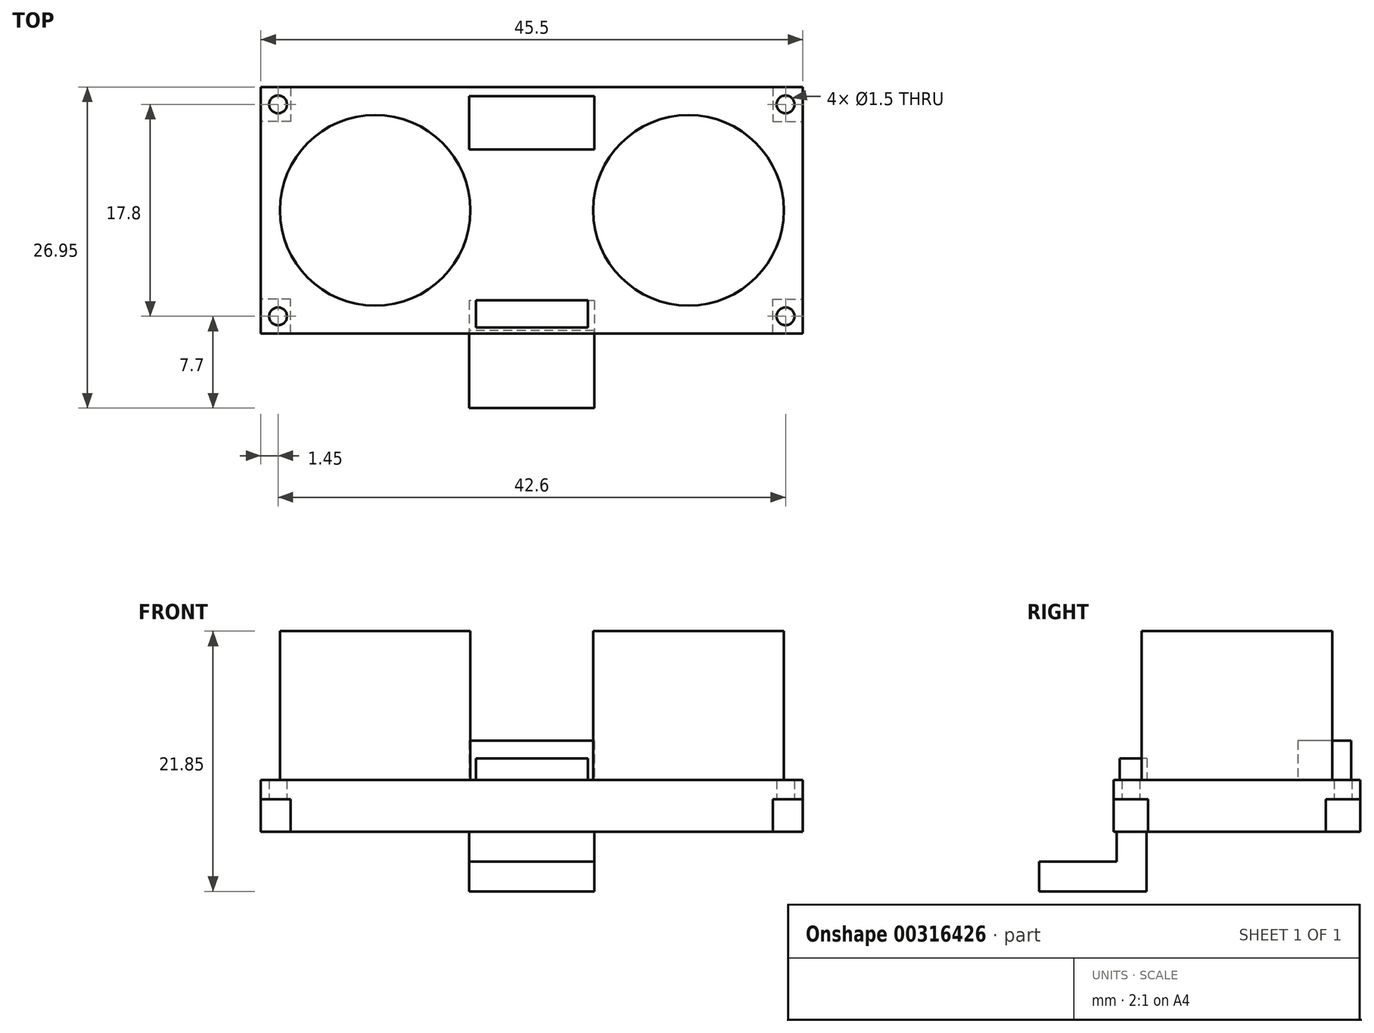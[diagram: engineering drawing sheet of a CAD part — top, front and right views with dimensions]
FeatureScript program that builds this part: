
annotation { "Feature Type Name" : "Feature", "Feature Type Description" : "" }
export const myFeature = defineFeature(function(context is Context, id is Id, definition is map)
    precondition{}
    {
        {
            var Q0;
            Q0=qCreatedBy(makeId("Top.planeOp"),FACE);
            var sketch = newSketch(context, id + "F0", { "sketchPlane" : qUnion([Q0])});
            skLineSegment(sketch, "E0.bottom", {"start": v(-22.75, 10.35) * mm, "end": v(22.75, 10.35) * mm});
            skLineSegment(sketch, "E0.top", {"start": v(-22.75, -10.35) * mm, "end": v(22.75, -10.35) * mm});
            skLineSegment(sketch, "E0.left", {"start": v(-22.75, 10.35) * mm, "end": v(-22.75, -10.35) * mm});
            skLineSegment(sketch, "E0.right", {"start": v(22.75, 10.35) * mm, "end": v(22.75, -10.35) * mm});
            skPoint(sketch, "E0.middle", {"position": v(0, 0) * mm});
            skCircle(sketch, "E1", {"center": v(-21.3, 8.9) * mm, "radius": 0.75 * mm});
            skCircle(sketch, "E2.MirrorC", {"center": v(21.3, 8.9) * mm, "radius": 0.75 * mm});
            skCircle(sketch, "E3.MirrorC", {"center": v(21.3, -8.9) * mm, "radius": 0.75 * mm});
            skCircle(sketch, "E4.MirrorC", {"center": v(-21.3, -8.9) * mm, "radius": 0.75 * mm});
            skSolve(sketch);
        }
        {
            var Q0;
            Q0 = qSketchRegion(id + "F0", true);
            extrude(context, id + "F1", {"entities" : qUnion([Q0]), "depth" : 1.6 * mm});
        }
        {
            var Q0;
            Q0=makeQuery(id+"F1.opExtrude","CAP_FACE",FACE,{"disambiguationData":[OSD([sQuery(id+"F0.wireOp",EDGE,"E0.bottom"),sQuery(id+"F0.wireOp",EDGE,"E0.top"),sQuery(id+"F0.wireOp",EDGE,"E0.left"),sQuery(id+"F0.wireOp",EDGE,"E0.right"),sQuery(id+"F0.wireOp",EDGE,"E1"),sQuery(id+"F0.wireOp",EDGE,"E2.MirrorC"),sQuery(id+"F0.wireOp",EDGE,"E3.MirrorC"),sQuery(id+"F0.wireOp",EDGE,"E4.MirrorC"),sQuery(id+"F0.wireOp",EDGE,"EcKcbucg-EIJj-1O6K-RH2d-xdvmN5E1ucRb"),sQuery(id+"F0.wireOp",EDGE,"HiSo9sqT-VgG6-14Ua-RjyV-KtrsNFatjuRK")])],"isStart":false});
            var sketch = newSketch(context, id + "F2", { "sketchPlane" : qUnion([Q0])});
            skCircle(sketch, "E5", {"center": v(-13.15, 0) * mm, "radius": 8 * mm});
            skCircle(sketch, "E6", {"center": v(13.15, 0) * mm, "radius": 8 * mm});
            skLineSegment(sketch, "E7.bottom", {"start": v(-5.25, 9.6) * mm, "end": v(5.25, 9.6) * mm});
            skLineSegment(sketch, "E7.top", {"start": v(-5.25, 5.1) * mm, "end": v(5.25, 5.1) * mm});
            skLineSegment(sketch, "E7.left", {"start": v(-5.25, 9.6) * mm, "end": v(-5.25, 5.1) * mm});
            skLineSegment(sketch, "E7.right", {"start": v(5.25, 9.6) * mm, "end": v(5.25, 5.1) * mm});
            skPoint(sketch, "E7.middle", {"position": v(0, 7.35) * mm});
            skLineSegment(sketch, "E8.bottom", {"start": v(-4.7, -7.55) * mm, "end": v(4.7, -7.55) * mm});
            skLineSegment(sketch, "E8.top", {"start": v(-4.7, -9.85) * mm, "end": v(4.7, -9.85) * mm});
            skLineSegment(sketch, "E8.left", {"start": v(-4.7, -7.55) * mm, "end": v(-4.7, -9.85) * mm});
            skLineSegment(sketch, "E8.right", {"start": v(4.7, -7.55) * mm, "end": v(4.7, -9.85) * mm});
            skPoint(sketch, "E8.middle", {"position": v(0, -8.7) * mm});
            skSolve(sketch);
        }
        {
            var Q0;
            Q0=makeQuery(id+"F2.imprint","IMPRINT",FACE,{"disambiguationData":[TD([[makeQuery(id+"F2.imprint","IMPRINT",EDGE,{"derivedFrom":sQuery(id+"F2.wireOp",EDGE,"E5")}),1.0]])]});
            var Q1;
            Q1=makeQuery(id+"F2.imprint","IMPRINT",FACE,{"disambiguationData":[TD([[makeQuery(id+"F2.imprint","IMPRINT",EDGE,{"derivedFrom":sQuery(id+"F2.wireOp",EDGE,"E6")}),1.0]])]});
            extrude(context, id + "F3", {"entities" : qUnion([Q0, Q1]), "operationType" : NewBodyOperationType.ADD, "depth" : 12.5 * mm});
        }
        {
            var Q0;
            Q0=makeQuery(id+"F2.imprint","IMPRINT",FACE,{"disambiguationData":[TD([[makeQuery(id+"F2.imprint","IMPRINT",EDGE,{"derivedFrom":sQuery(id+"F2.wireOp",EDGE,"E7.bottom")}),-1.0]])]});
            extrude(context, id + "F4", {"entities" : qUnion([Q0]), "operationType" : NewBodyOperationType.ADD, "depth" : 3.3 * mm});
        }
        {
            var Q0;
            Q0=makeQuery(id+"F2.imprint","IMPRINT",FACE,{"disambiguationData":[TD([[makeQuery(id+"F2.imprint","IMPRINT",EDGE,{"derivedFrom":sQuery(id+"F2.wireOp",EDGE,"E8.bottom")}),-1.0]])]});
            extrude(context, id + "F5", {"entities" : qUnion([Q0]), "operationType" : NewBodyOperationType.ADD, "depth" : 1.8 * mm});
        }
        {
            var Q0;
            Q0=makeQuery(id+"F1.opExtrude","CAP_FACE",FACE,{"disambiguationData":[OSD([sQuery(id+"F0.wireOp",EDGE,"E0.bottom"),sQuery(id+"F0.wireOp",EDGE,"E0.top"),sQuery(id+"F0.wireOp",EDGE,"E0.left"),sQuery(id+"F0.wireOp",EDGE,"E0.right"),sQuery(id+"F0.wireOp",EDGE,"E1"),sQuery(id+"F0.wireOp",EDGE,"E2.MirrorC"),sQuery(id+"F0.wireOp",EDGE,"E3.MirrorC"),sQuery(id+"F0.wireOp",EDGE,"E4.MirrorC")])],"isStart":true});
            var sketch = newSketch(context, id + "F6", { "sketchPlane" : qUnion([Q0])});
            skLineSegment(sketch, "E9", {"start": v(-20.25, -10.35) * mm, "end": v(-20.25, -7.45) * mm});
            skLineSegment(sketch, "E10", {"start": v(-20.25, -7.45) * mm, "end": v(-22.75, -7.45) * mm});
            skLineSegment(sketch, "E11.MirrorCS", {"start": v(-20.25, 7.45) * mm, "end": v(-22.75, 7.45) * mm});
            skLineSegment(sketch, "E12.MirrorCS", {"start": v(-20.25, 10.35) * mm, "end": v(-20.25, 7.45) * mm});
            skLineSegment(sketch, "E13.MirrorCS", {"start": v(20.25, 10.35) * mm, "end": v(20.25, 7.45) * mm});
            skLineSegment(sketch, "E14.MirrorCS", {"start": v(20.25, 7.45) * mm, "end": v(22.75, 7.45) * mm});
            skLineSegment(sketch, "E15.MirrorCS", {"start": v(20.25, -10.35) * mm, "end": v(20.25, -7.45) * mm});
            skLineSegment(sketch, "E16.MirrorCS", {"start": v(20.25, -7.45) * mm, "end": v(22.75, -7.45) * mm});
            skSolve(sketch);
        }
        {
            var Q0;
            {var subQ6=sQuery(id+"F6.wireOp",EDGE,"E9");Q0=makeQuery(id+"F6.imprint","IMPRINT",FACE,{"disambiguationData":[TD([[makeQuery(id+"F6.imprint","IMPRINT",EDGE,{"derivedFrom":subQ6}),-1.0]])]});}
            extrude(context, id + "F7", {"entities" : qUnion([Q0]), "operationType" : NewBodyOperationType.ADD, "depth" : 2.75 * mm});
        }
        {
            var Q0;
            Q0=makeQuery(id+"F7.opExtrude","CAP_FACE",FACE,{"disambiguationData":[OSD([sQuery(id+"F0.wireOp",EDGE,"E0.bottom"),sQuery(id+"F0.wireOp",EDGE,"E0.top"),sQuery(id+"F0.wireOp",EDGE,"E0.left"),sQuery(id+"F0.wireOp",EDGE,"E0.right"),sQuery(id+"F6.wireOp",EDGE,"E9"),sQuery(id+"F6.wireOp",EDGE,"E10"),sQuery(id+"F6.wireOp",EDGE,"E11.MirrorCS"),sQuery(id+"F6.wireOp",EDGE,"E12.MirrorCS"),sQuery(id+"F6.wireOp",EDGE,"E13.MirrorCS"),sQuery(id+"F6.wireOp",EDGE,"E14.MirrorCS"),sQuery(id+"F6.wireOp",EDGE,"E15.MirrorCS"),sQuery(id+"F6.wireOp",EDGE,"E16.MirrorCS")])],"isStart":false});
            var sketch = newSketch(context, id + "F8", { "sketchPlane" : qUnion([Q0])});
            skLineSegment(sketch, "E17.bottom", {"start": v(5.25, 7.6) * mm, "end": v(-5.25, 7.6) * mm});
            skLineSegment(sketch, "E17.top", {"start": v(5.25, 10.1) * mm, "end": v(-5.25, 10.1) * mm});
            skLineSegment(sketch, "E17.left", {"start": v(5.25, 7.6) * mm, "end": v(5.25, 10.1) * mm});
            skLineSegment(sketch, "E17.right", {"start": v(-5.25, 7.6) * mm, "end": v(-5.25, 10.1) * mm});
            skSolve(sketch);
        }
        {
            var Q0;
            Q0=makeQuery(id+"F8.imprint","IMPRINT",FACE,{"disambiguationData":[TD([[makeQuery(id+"F8.imprint","IMPRINT",EDGE,{"derivedFrom":sQuery(id+"F8.wireOp",EDGE,"E17.bottom")}),-1.0]])]});
            extrude(context, id + "F9", {"entities" : qUnion([Q0]), "operationType" : NewBodyOperationType.ADD, "depth" : 5 * mm});
        }
        {
            var Q0;
            Q0=makeQuery(id+"F9.opExtrude","SWEPT_FACE",FACE,{"disambiguationData":[OSD([sQuery(id+"F8.wireOp",EDGE,"E17.top")])]});
            var sketch = newSketch(context, id + "F10", { "sketchPlane" : qUnion([Q0])});
            skLineSegment(sketch, "E18.bottom", {"start": v(-5.25, -7.75) * mm, "end": v(5.25, -7.75) * mm});
            skLineSegment(sketch, "E18.top", {"start": v(-5.25, -5.25) * mm, "end": v(5.25, -5.25) * mm});
            skLineSegment(sketch, "E18.left", {"start": v(-5.25, -7.75) * mm, "end": v(-5.25, -5.25) * mm});
            skLineSegment(sketch, "E18.right", {"start": v(5.25, -7.75) * mm, "end": v(5.25, -5.25) * mm});
            skSolve(sketch);
        }
        {
            var Q0;
            Q0=makeQuery(id+"F10.imprint","IMPRINT",FACE,{"disambiguationData":[TD([[makeQuery(id+"F10.imprint","IMPRINT",EDGE,{"derivedFrom":sQuery(id+"F10.wireOp",EDGE,"E18.bottom")}),-1.0]])]});
            extrude(context, id + "F11", {"entities" : qUnion([Q0]), "operationType" : NewBodyOperationType.ADD, "depth" : 6.5 * mm});
        }
    });
